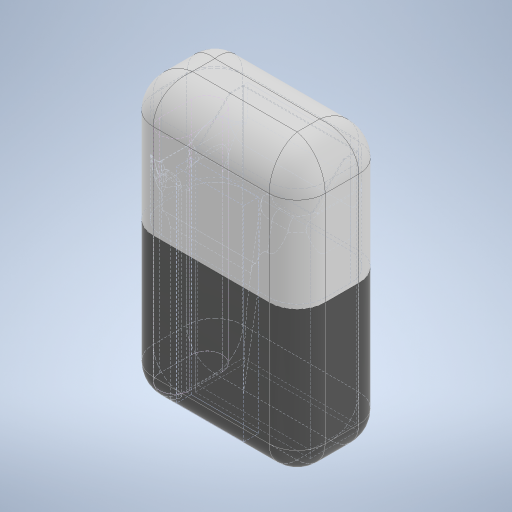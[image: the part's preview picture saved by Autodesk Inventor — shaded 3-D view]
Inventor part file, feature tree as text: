
AUTODESK INVENTOR PART (.ipt)
format: ipt  version: 2023 (Build 270158030, 158C)  size: 1,090,048 bytes
history: native  units: mm
features: fillet x15, sketch x15, extrude x14, other x5, chamfer x1
ambient origin geometry x8: Origin, YZ Plane, XZ Plane, XY Plane, X Axis, Y Axis, Z Axis, Center Point
bodies: Solid7 (feature_tree)
feature tree (50):
  other  "filtercase"
  extrude  "Extrusion1"  Depth=40.97mm
  extrude  "Extrusion2"  Depth=0.32mm
  extrude  "Extrusion3"  Depth=0.32mm
  extrude  "Extrusion4"  Depth=84.0mm TaperAngle=0.0deg
  extrude  "Extrusion5"  Depth=5.0mm
  extrude  "Extrusion6"  Depth=5.1mm
  extrude  "Extrusion7"  Depth=1.5mm
  extrude  "Extrusion8"  Depth=10.0mm TaperAngle=0.0deg
  extrude  "Extrusion9"  Depth=5.3mm
  extrude  "Extrusion10"  Depth=10.75mm
  chamfer  "Chamfer1"  Distance=78.88mm
  fillet  "Fillet2"  Radius=3.0mm
  fillet  "Fillet3"  Radius=3.0mm
  fillet  "Fillet4"  Radius=78.88mm
  fillet  "Fillet5"  Radius=3.0mm
  fillet  "Fillet6"  Radius=1.55mm
  fillet  "Fillet7"  Radius=1.55mm
  fillet  "Fillet8"  Radius=1.55mm
  fillet  "Fillet9"  Radius=1.55mm
  fillet  "Fillet10"  Radius=25.0mm
  fillet  "Fillet11"  Radius=2.0mm
  fillet  "Fillet12"  [1 undecoded]
  fillet  "Fillet13"  Radius=10.0mm
  sketch  "Sketch12"  dims[d25=22.26mm]
  extrude  "Extrusion11"  Depth=10.0mm
  extrude  "Extrusion12"  Depth=10.0mm
  fillet  "Fillet14"  Radius=10.0mm
  sketch  "Sketch15"  dims[d28=-5.815mm]
  fillet  "Fillet15"  Radius=10.0mm
  extrude  "Extrusion13"  Depth=10.0mm
  extrude  "Extrusion14"  Depth=10.0mm
  fillet  "Fillet16"  Radius=13.0mm
  sketch  "Sketch1"  dims[d0=17.1mm d1=40.97mm]
  sketch  "Sketch2"  dims[d2=86.3mm d3=0.0mm d4=0.32mm]
  sketch  "Sketch3"  dims[d5=0.32mm d6=0.32mm]
  sketch  "Sketch4"  dims[d7=0.32mm d8=84.0mm d9=0.0mm]
  other  "roll-buddy-body"
  sketch  "Sketch5"  dims[d10=1.3mm d11=5.0mm]
  other  "rizler"
  sketch  "Sketch7"  dims[d12=0.0mm d13=0.0mm d14=5.1mm]
  other  "cricket"
  sketch  "Sketch8"  dims[d15=1.5mm d16=1.5mm]
  sketch  "Sketch9"  dims[d17=5.1mm d18=10.0mm d19=0.0mm]
  sketch  "Sketch10"  dims[d20=24.0mm d21=5.3mm]
  sketch  "Sketch11"  dims[d22=73.0mm d23=0.0mm d24=10.75mm]
  sketch  "Sketch13"  dims[d26=1.0mm]
  sketch  "Sketch14"  dims[d27=11.19mm]
  other  "lid"
  sketch  "Sketch16"  dims[d29=0.925mm d30=78.88mm d31=0.0mm d32=3.0mm d33=3.0mm d34=78.88mm d35=0.0mm d36=3.0mm d37=0.0mm d38=1.55mm d39=1.55mm d40=1.55mm d41=1.55mm d42=25.0mm d43=0.0mm d44=2.0mm d45=2.0mm d46=13.962634mm d48=0.0mm d49=0.0mm d51=10.0mm d52=8.0mm d53=10.0mm d54=10.0mm d55=10.0mm d56=10.0mm d57=10.0mm d58=13.0mm d59=13.0mm d60=1.0mm d61=1.0mm d62=0.1mm d63=0.1mm d64=1.122mm d65=0.0mm d66=1.122mm d67=0.0mm d68=4.35mm d69=1.5mm d70=1.5mm d71=1.5mm d72=1.5mm d73=3.0mm d74=10.0mm d75=10.0mm d76=0.0mm d77=10.0mm d78=0.0mm d79=12.0mm]
note: 1 required parameter value undecoded (feature->parameter linkage not recoverable at this tier; creation-order binding heuristic only, values carry confidence <= 0.55)
